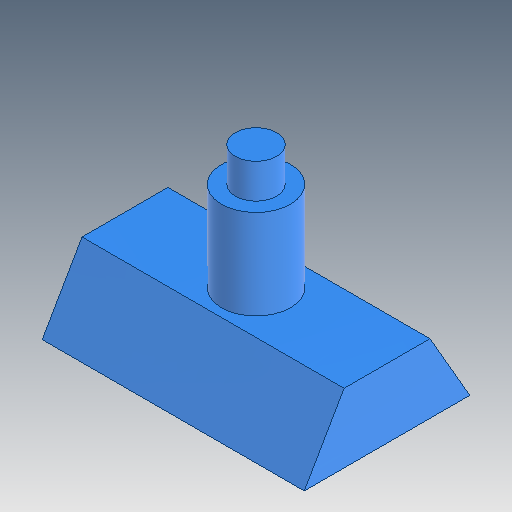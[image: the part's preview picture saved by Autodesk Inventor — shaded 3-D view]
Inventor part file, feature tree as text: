
AUTODESK INVENTOR PART (.ipt)
format: ipt  version: 2017 (Build 210142000, 142)  size: 99,328 bytes
history: native  units: mm
features: extrude x3, sketch x3
ambient origin geometry x8: Origin, YZ Plane, XZ Plane, XY Plane, X Axis, Y Axis, Z Axis, Center Point
bodies: Body1 (feature_tree)
feature tree (6):
  extrude  "Extrusion3"  TaperAngle=60.0deg  [1 undecoded]
  extrude  "Extrusion4"  Depth=12.0mm
  extrude  "Extrusion5"  Depth=10.0mm
  sketch  "Sketch4"  dims[d31=60.0deg d32=60.0deg]
  sketch  "Sketch5"  dims[d33=10.0mm d34=12.0mm]
  sketch  "Sketch6"  dims[d35=38.0mm d36=0.0mm d37=10.0mm d38=13.0mm d39=0.0mm d40=6.0mm d41=5.0mm d42=0.0mm]
note: 1 required parameter value undecoded (feature->parameter linkage not recoverable at this tier; creation-order binding heuristic only, values carry confidence <= 0.55)
